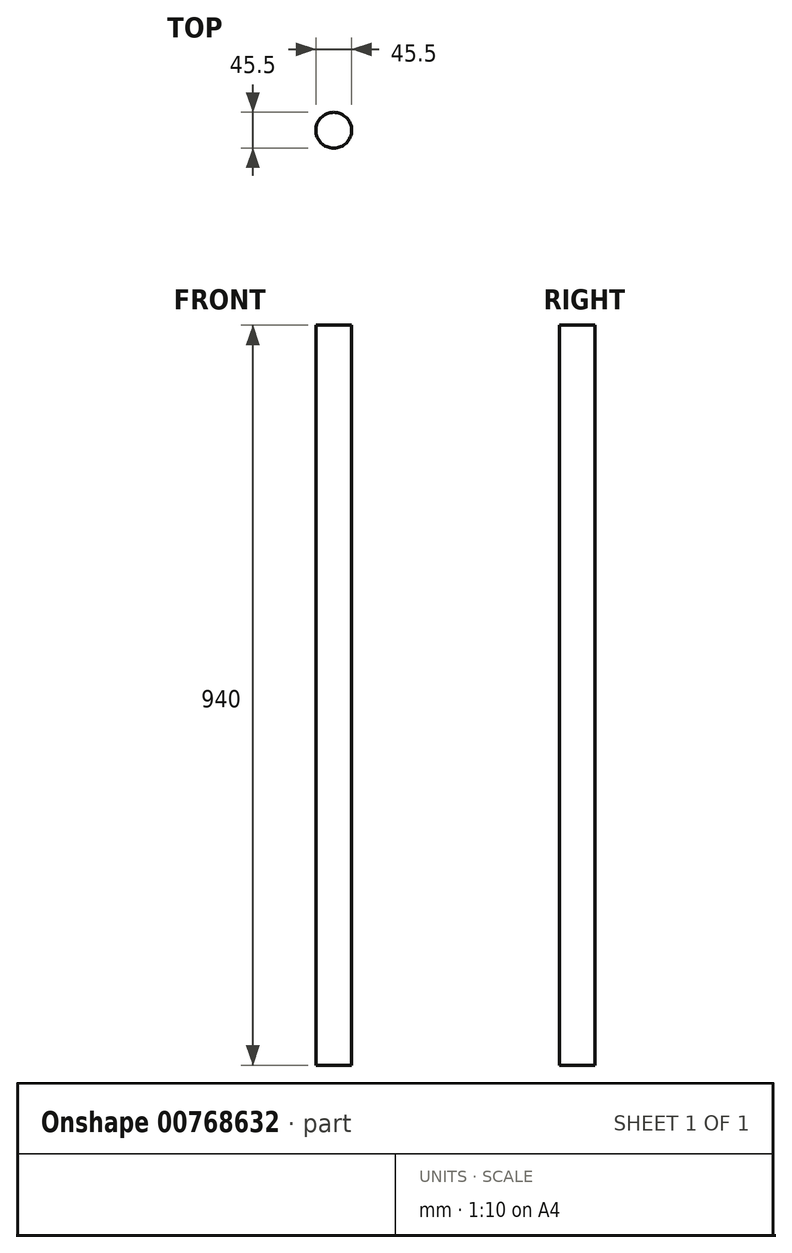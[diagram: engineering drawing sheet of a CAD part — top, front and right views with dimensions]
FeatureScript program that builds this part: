
annotation { "Feature Type Name" : "Feature", "Feature Type Description" : "" }
export const myFeature = defineFeature(function(context is Context, id is Id, definition is map)
    precondition{}
    {
        {
            var Q0;
            Q0=qCreatedBy(makeId("Top.planeOp"),FACE);
            var sketch = newSketch(context, id + "F0", { "sketchPlane" : qUnion([Q0])});
            skCircle(sketch, "E0", {"center": v(0, 0) * mm, "radius": 24.75 * mm});
            skCircle(sketch, "E1", {"center": v(0, 0) * mm, "radius": 22.75 * mm});
            skSolve(sketch);
        }
        {
            var Q0;
            Q0=sQuery(id+"F0.wireOp",EDGE,"E1");
            extrude(context, id + "F1", {"bodyType" : ToolBodyType.SURFACE, "surfaceEntities" : qUnion([Q0]), "depth" : 940 * mm, "offsetDistance" : 25 * mm});
        }
    });
